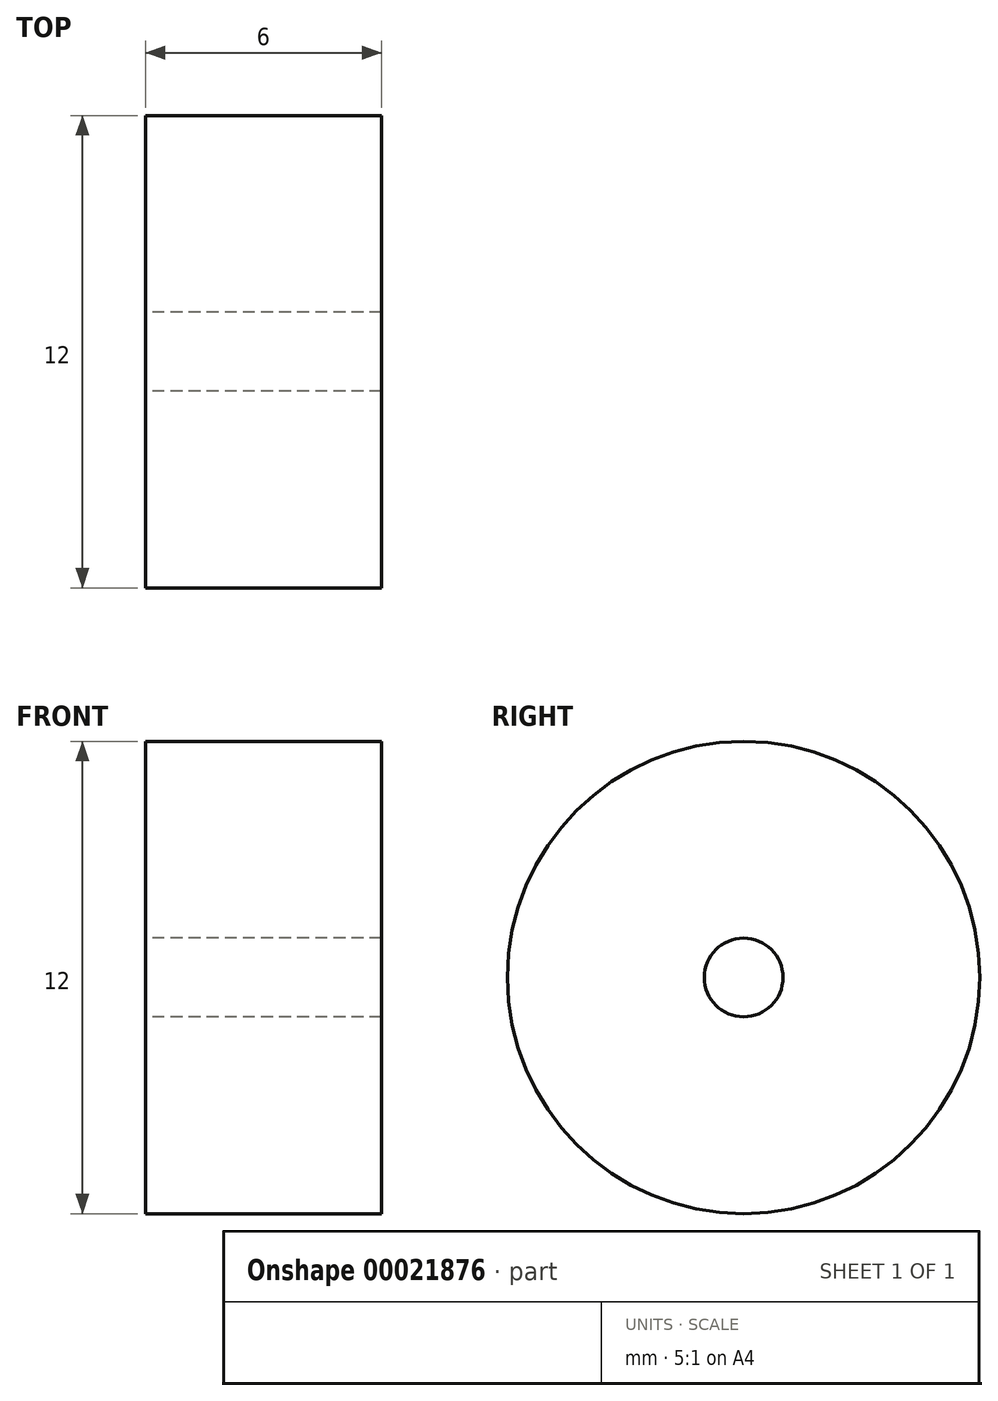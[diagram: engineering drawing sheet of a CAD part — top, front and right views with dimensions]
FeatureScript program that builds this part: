
annotation { "Feature Type Name" : "Feature", "Feature Type Description" : "" }
export const myFeature = defineFeature(function(context is Context, id is Id, definition is map)
    precondition{}
    {
        {
            var Q0;
            Q0=qCreatedBy(makeId("Right.planeOp"),FACE);
            var sketch = newSketch(context, id + "F0", { "sketchPlane" : qUnion([Q0])});
            skCircle(sketch, "E0", {"center": v(59.3, 13.26) * mm, "radius": 6 * mm});
            skCircle(sketch, "E1", {"center": v(59.3, 13.26) * mm, "radius": 1 * mm});
            skSolve(sketch);
        }
        {
            var Q0;
            Q0 = qSketchRegion(id + "F0", true);
            extrude(context, id + "F1", {"entities" : qUnion([Q0]), "depth" : 6 * mm});
        }
        {
            var Q0;
            Q0=makeQuery(id+"F1.opExtrude","SWEPT_BODY",BODY,{"disambiguationData":[OSD([sQuery(id+"F0.wireOp",EDGE,"E0"),sQuery(id+"F0.wireOp",EDGE,"E1")])]});
            transform(context, id + "F2", {"entities" : qUnion([Q0]), "transformType" : TransformType.TRANSLATION_3D, "dx" : 0 * mm, "dy" : 0 * mm, "dz" : 0 * mm, "makeCopy" : true});
        }
    });
